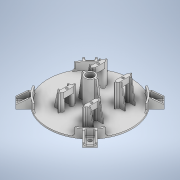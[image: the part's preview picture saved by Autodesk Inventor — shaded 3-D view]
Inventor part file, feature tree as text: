
AUTODESK INVENTOR PART (.ipt)
format: ipt  version: 2021 (Build 250183000, 183)  size: 586,240 bytes
history: native  units: mm
features: sketch x14, extrude x10, projected_geometry x9, plane x7, mirror x7, rib x6, fillet x2, shell x1, hole x1, chamfer x1, pattern_circular x1
ambient origin geometry x8: Origin, YZ Plane, XZ Plane, XY Plane, X Axis, Y Axis, Z Axis, Center Point
bodies: Solid1 (feature_tree)
feature tree (59):
  extrude  "Extrusion1"  Depth=10.0mm TaperAngle=0.0deg
  shell  "Shell1"  Thickness=1.6mm
  sketch  "Sketch2"  dims[d15=27.699569mm d16=23.050635mm]
  extrude  "Extrusion2"  Depth=27.699569mm
  extrude  "Extrusion3"  Depth=5.397284mm
  extrude  "Extrusion4"  Depth=24.511291mm
  extrude  "Extrusion5"  Depth=5.397219mm
  extrude  "Extrusion6"  Depth=19.05mm TaperAngle=0.0deg
  extrude  "Extrusion7"  TaperAngle=0.0deg  [1 undecoded]
  extrude  "Extrusion8"  Depth=6.35mm TaperAngle=0.0deg
  plane  "Work Plane2"
  plane  "Work Plane4"
  rib  "Rib1"
  plane  "Work Plane5"
  rib  "Rib2"
  plane  "Work Plane7"
  rib  "Rib5"
  rib  "Rib6"
  mirror  "Mirror3"
  mirror  "Mirror4"
  mirror  "Mirror5"
  rib  "Rib7"
  mirror  "Mirror6"
  extrude  "Extrusion9"  Depth=6.35mm
  rib  "Rib8"
  plane  "Work Plane8"
  mirror  "Mirror7"
  fillet  "Fillet1"  Radius=5.397mm
  mirror  "Mirror8"
  mirror  "Mirror9"
  hole  "Hole1"  [1 undecoded]
  fillet  "Fillet2"  Radius=2.0mm
  extrude  "Extrusion10"  Depth=2.0mm
  chamfer  "Chamfer1"  Distance=6.0mm
  pattern_circular  "Circular Pattern1"  [2 undecoded]
  sketch  "Sketch1"  dims[d0=94.0mm d1=10.0mm d2=0.0mm d3=1.6mm]
  sketch  "Sketch3"  dims[d17=8.39516mm d18=5.397284mm]
  projected_geometry  "Projected Loop1"
  projected_geometry  "Projected Loop2"
  projected_geometry  "Projected Loop3"
  projected_geometry  "Projected Loop4"
  sketch  "Sketch4"  dims[d19=5.397605mm d20=24.511291mm]
  sketch  "Sketch5"  dims[d21=5.397555mm d22=5.397219mm]
  plane  "Work Plane1"
  plane  "Work Plane3"
  sketch  "Sketch6"  dims[d23=27.313mm d24=0.0mm d25=19.05mm d26=0.0mm]
  projected_geometry  "Projected Loop5"
  projected_geometry  "Projected Loop6"
  projected_geometry  "Projected Loop7"
  projected_geometry  "Projected Loop8"
  sketch  "Sketch7"  dims[d27=6.35mm d28=0.0mm d29=0.0mm d30=0.0mm]
  projected_geometry  "Projected Loop9"
  sketch  "Sketch9"  dims[d31=25.4mm d32=0.0mm d33=6.35mm d34=0.0mm]
  sketch  "Sketch10"  dims[d35=6.35mm d36=0.0mm d37=23.05mm d38=-5.397mm d39=-23.05mm d40=5.397mm]
  sketch  "Sketch11"  dims[d42=6.0mm d43=2.0mm]
  sketch  "Sketch12"  dims[d44=1.0mm d45=1.0mm d46=0.0mm d47=0.0mm d48=1.0mm d49=1.0mm d50=2.0mm]
  sketch  "Sketch13"  dims[d51=6.0mm d52=2.0mm]
  sketch  "Sketch14"  dims[d53=2.0mm]
  sketch  "Sketch15"  dims[d54=5.999704mm d55=6.0mm d56=2.0mm d57=6.0mm d58=1.0mm d59=1.0mm d60=0.0mm d61=0.0mm d62=1.0mm d63=1.0mm d80=2.0mm d81=1.0mm d82=1.0mm d83=0.0mm d84=0.0mm d85=1.0mm d86=1.0mm d87=2.0mm d88=1.0mm d89=1.0mm d90=0.0mm d91=0.0mm d92=1.0mm d93=1.0mm d94=2.0mm d95=6.0mm d96=1.0mm d97=2.0mm d98=0.0mm d99=0.0mm d100=1.0mm d101=1.0mm d103=45.0deg d104=45.0deg d105=12.0mm d106=12.0mm d107=2.5mm d108=0.0mm d109=2.0mm d110=2.0mm d111=1.0mm d112=2.0mm d113=0.0mm d114=0.0mm d115=1.0mm d116=1.0mm d117=1.0mm d122=4.0mm d123=6.0mm d124=4.0mm d125=2.0mm d126=90.0deg d127=8.0mm d128=20.594885mm d129=8.5mm d130=11.8mm d131=1.0mm d132=94.0mm d133=90.8mm d134=30.0deg d135=30.0deg d136=10.0mm d137=0.0mm d138=2.0mm d139=2.0mm d140=45.0deg d141=40.0mm d142=360.0deg d144=105.0mm d145=45.0deg d146=40.0mm d148=360.0deg]
note: 4 required parameter values undecoded (feature->parameter linkage not recoverable at this tier; creation-order binding heuristic only, values carry confidence <= 0.55)
